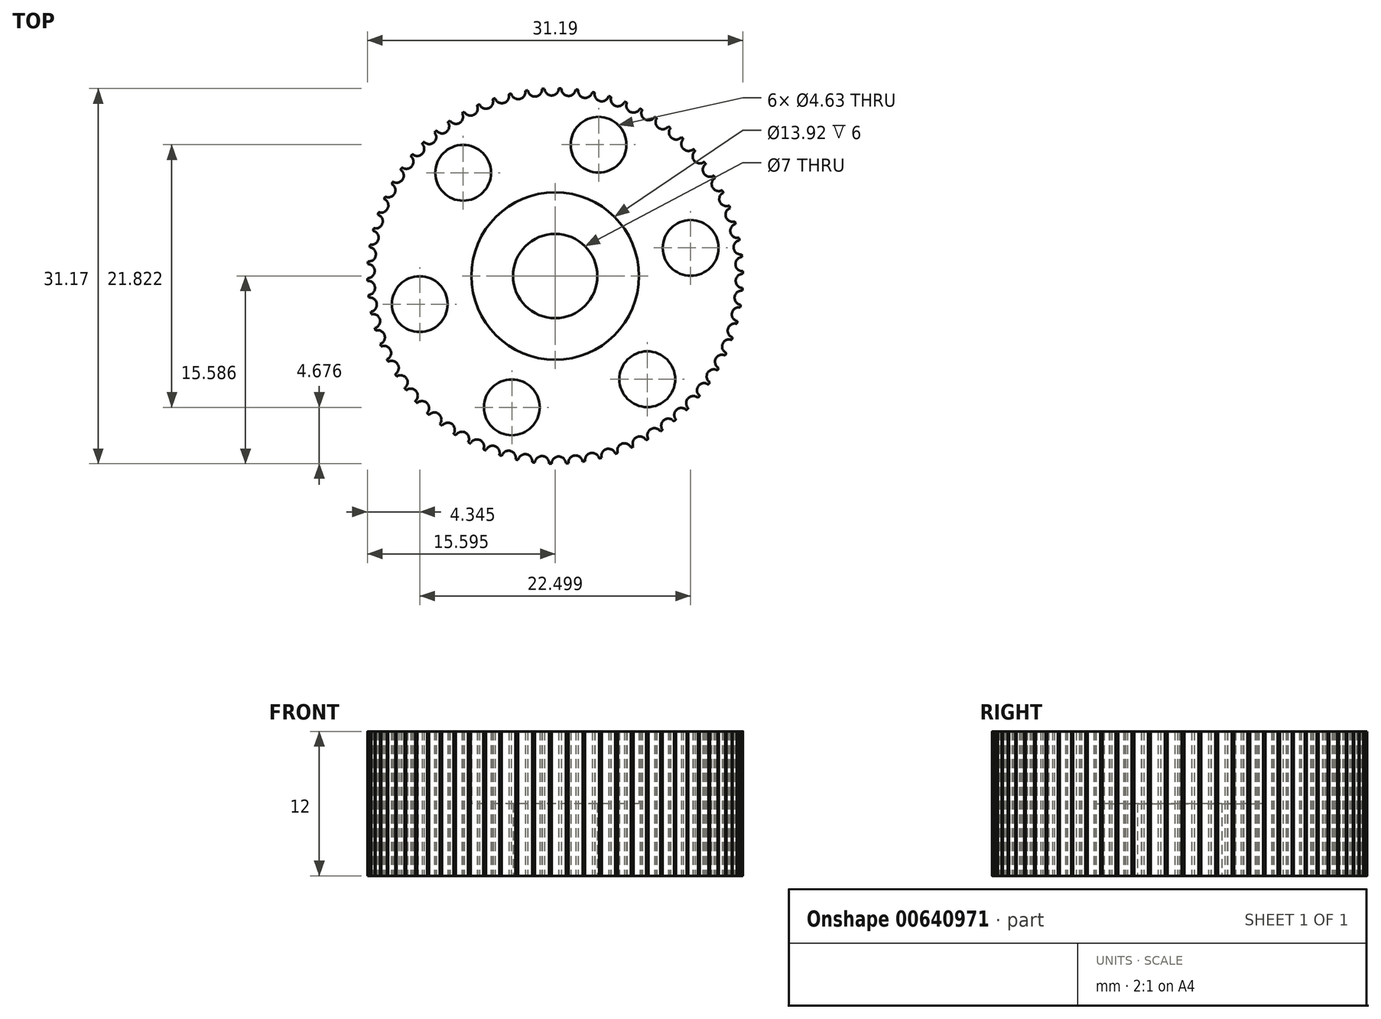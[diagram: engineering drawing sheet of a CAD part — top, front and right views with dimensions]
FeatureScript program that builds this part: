
annotation { "Feature Type Name" : "Feature", "Feature Type Description" : "" }
export const myFeature = defineFeature(function(context is Context, id is Id, definition is map)
    precondition{}
    {
        {
            var Q0;
            Q0=qCreatedBy(makeId("Top.planeOp"),FACE);
            var sketch = newSketch(context, id + "F0", { "sketchPlane" : qUnion([Q0])});
            skCircle(sketch, "E0", {"center": v(-13.85, 5.29) * mm, "radius": 0.6 * mm});
            skCircle(sketch, "E1.1.0", {"center": v(-14.2, 3.93) * mm, "radius": 0.6 * mm});
            skCircle(sketch, "E1.2.0", {"center": v(-14.42, 2.55) * mm, "radius": 0.6 * mm});
            skCircle(sketch, "E1.3.0", {"center": v(-14.52, 1.16) * mm, "radius": 0.6 * mm});
            skCircle(sketch, "E1.4.0", {"center": v(-14.5, -0.24) * mm, "radius": 0.6 * mm});
            skCircle(sketch, "E1.5.0", {"center": v(-14.34, -1.63) * mm, "radius": 0.6 * mm});
            skCircle(sketch, "E1.6.0", {"center": v(-14.07, -3) * mm, "radius": 0.6 * mm});
            skCircle(sketch, "E1.7.0", {"center": v(-13.67, -4.35) * mm, "radius": 0.6 * mm});
            skCircle(sketch, "E1.8.0", {"center": v(-13.15, -5.65) * mm, "radius": 0.6 * mm});
            skCircle(sketch, "E1.9.0", {"center": v(-12.52, -6.9) * mm, "radius": 0.6 * mm});
            skCircle(sketch, "E1.10.0", {"center": v(-11.78, -8.08) * mm, "radius": 0.6 * mm});
            skCircle(sketch, "E1.11.0", {"center": v(-10.94, -9.2) * mm, "radius": 0.6 * mm});
            skCircle(sketch, "E1.12.0", {"center": v(-10, -10.24) * mm, "radius": 0.6 * mm});
            skCircle(sketch, "E1.13.0", {"center": v(-8.97, -11.18) * mm, "radius": 0.6 * mm});
            skCircle(sketch, "E1.14.0", {"center": v(-7.86, -12.04) * mm, "radius": 0.6 * mm});
            skCircle(sketch, "E1.15.0", {"center": v(-6.68, -12.78) * mm, "radius": 0.6 * mm});
            skCircle(sketch, "E1.16.0", {"center": v(-5.44, -13.42) * mm, "radius": 0.6 * mm});
            skCircle(sketch, "E1.17.0", {"center": v(-4.14, -13.95) * mm, "radius": 0.6 * mm});
            skCircle(sketch, "E1.18.0", {"center": v(-2.8, -14.36) * mm, "radius": 0.6 * mm});
            skCircle(sketch, "E1.19.0", {"center": v(-1.43, -14.64) * mm, "radius": 0.6 * mm});
            skCircle(sketch, "E1.20.0", {"center": v(-0.04, -14.8) * mm, "radius": 0.6 * mm});
            skCircle(sketch, "E1.21.0", {"center": v(1.36, -14.84) * mm, "radius": 0.6 * mm});
            skCircle(sketch, "E1.22.0", {"center": v(2.75, -14.75) * mm, "radius": 0.6 * mm});
            skCircle(sketch, "E1.23.0", {"center": v(4.13, -14.54) * mm, "radius": 0.6 * mm});
            skCircle(sketch, "E1.24.0", {"center": v(5.5, -14.2) * mm, "radius": 0.6 * mm});
            skCircle(sketch, "E1.25.0", {"center": v(6.81, -13.75) * mm, "radius": 0.6 * mm});
            skCircle(sketch, "E1.26.0", {"center": v(8.1, -13.17) * mm, "radius": 0.6 * mm});
            skCircle(sketch, "E1.27.0", {"center": v(9.31, -12.49) * mm, "radius": 0.6 * mm});
            skCircle(sketch, "E1.28.0", {"center": v(10.46, -11.7) * mm, "radius": 0.6 * mm});
            skCircle(sketch, "E1.29.0", {"center": v(11.54, -10.8) * mm, "radius": 0.6 * mm});
            skCircle(sketch, "E1.30.0", {"center": v(12.53, -9.82) * mm, "radius": 0.6 * mm});
            skCircle(sketch, "E1.31.0", {"center": v(13.43, -8.75) * mm, "radius": 0.6 * mm});
            skCircle(sketch, "E1.32.0", {"center": v(14.24, -7.6) * mm, "radius": 0.6 * mm});
            skCircle(sketch, "E1.33.0", {"center": v(14.93, -6.38) * mm, "radius": 0.6 * mm});
            skCircle(sketch, "E1.34.0", {"center": v(15.51, -5.11) * mm, "radius": 0.6 * mm});
            skCircle(sketch, "E1.35.0", {"center": v(15.98, -3.8) * mm, "radius": 0.6 * mm});
            skCircle(sketch, "E1.36.0", {"center": v(16.33, -2.44) * mm, "radius": 0.6 * mm});
            skCircle(sketch, "E1.37.0", {"center": v(16.55, -1.06) * mm, "radius": 0.6 * mm});
            skCircle(sketch, "E1.38.0", {"center": v(16.65, 0.34) * mm, "radius": 0.6 * mm});
            skCircle(sketch, "E1.39.0", {"center": v(16.62, 1.74) * mm, "radius": 0.6 * mm});
            skCircle(sketch, "E1.40.0", {"center": v(16.47, 3.13) * mm, "radius": 0.6 * mm});
            skCircle(sketch, "E1.41.0", {"center": v(16.2, 4.5) * mm, "radius": 0.6 * mm});
            skCircle(sketch, "E1.42.0", {"center": v(15.8, 5.84) * mm, "radius": 0.6 * mm});
            skCircle(sketch, "E1.43.0", {"center": v(15.28, 7.14) * mm, "radius": 0.6 * mm});
            skCircle(sketch, "E1.44.0", {"center": v(14.65, 8.39) * mm, "radius": 0.6 * mm});
            skCircle(sketch, "E1.45.0", {"center": v(13.91, 9.58) * mm, "radius": 0.6 * mm});
            skCircle(sketch, "E1.46.0", {"center": v(13.07, 10.7) * mm, "radius": 0.6 * mm});
            skCircle(sketch, "E1.47.0", {"center": v(12.13, 11.73) * mm, "radius": 0.6 * mm});
            skCircle(sketch, "E1.48.0", {"center": v(11.1, 12.68) * mm, "radius": 0.6 * mm});
            skCircle(sketch, "E1.49.0", {"center": v(10, 13.53) * mm, "radius": 0.6 * mm});
            skCircle(sketch, "E1.50.0", {"center": v(8.81, 14.28) * mm, "radius": 0.6 * mm});
            skCircle(sketch, "E1.51.0", {"center": v(7.57, 14.92) * mm, "radius": 0.6 * mm});
            skCircle(sketch, "E1.52.0", {"center": v(6.27, 15.44) * mm, "radius": 0.6 * mm});
            skCircle(sketch, "E1.53.0", {"center": v(4.93, 15.85) * mm, "radius": 0.6 * mm});
            skCircle(sketch, "E1.54.0", {"center": v(3.56, 16.14) * mm, "radius": 0.6 * mm});
            skCircle(sketch, "E1.55.0", {"center": v(2.17, 16.3) * mm, "radius": 0.6 * mm});
            skCircle(sketch, "E1.56.0", {"center": v(0.77, 16.33) * mm, "radius": 0.6 * mm});
            skCircle(sketch, "E1.57.0", {"center": v(-0.62, 16.25) * mm, "radius": 0.6 * mm});
            skCircle(sketch, "E1.58.0", {"center": v(-2, 16.03) * mm, "radius": 0.6 * mm});
            skCircle(sketch, "E1.59.0", {"center": v(-3.36, 15.7) * mm, "radius": 0.6 * mm});
            skCircle(sketch, "E1.60.0", {"center": v(-4.68, 15.24) * mm, "radius": 0.6 * mm});
            skCircle(sketch, "E1.61.0", {"center": v(-5.96, 14.66) * mm, "radius": 0.6 * mm});
            skCircle(sketch, "E1.62.0", {"center": v(-7.18, 13.98) * mm, "radius": 0.6 * mm});
            skCircle(sketch, "E1.63.0", {"center": v(-8.33, 13.19) * mm, "radius": 0.6 * mm});
            skCircle(sketch, "E1.64.0", {"center": v(-9.41, 12.3) * mm, "radius": 0.6 * mm});
            skCircle(sketch, "E1.65.0", {"center": v(-10.4, 11.3) * mm, "radius": 0.6 * mm});
            skCircle(sketch, "E1.66.0", {"center": v(-11.3, 10.24) * mm, "radius": 0.6 * mm});
            skCircle(sketch, "E1.67.0", {"center": v(-12.1, 9.1) * mm, "radius": 0.6 * mm});
            skCircle(sketch, "E1.68.0", {"center": v(-12.8, 7.88) * mm, "radius": 0.6 * mm});
            skCircle(sketch, "E1.69.0", {"center": v(-13.38, 6.6) * mm, "radius": 0.6 * mm});
            skPoint(sketch, "E1.center", {"position": v(1.07, 0.75) * mm});
            skCircle(sketch, "E2", {"center": v(1.07, 0.75) * mm, "radius": 15.6 * mm});
            skCircle(sketch, "E3", {"center": v(1.07, 0.75) * mm, "radius": 3.5 * mm});
            skPoint(sketch, "E4.2.0", {"position": v(0, 0) * mm});
            skPoint(sketch, "E4.3.0", {"position": v(0, 0) * mm});
            skPoint(sketch, "E4.6.0", {"position": v(0, 0) * mm});
            skCircle(sketch, "E5", {"center": v(1.07, 0.75) * mm, "radius": 6.96 * mm});
            skCircle(sketch, "E6", {"center": v(-6.58, 9.32) * mm, "radius": 2.32 * mm});
            skCircle(sketch, "E7.1.0", {"center": v(-10.18, -1.6) * mm, "radius": 2.32 * mm});
            skCircle(sketch, "E7.2.0", {"center": v(-2.54, -10.16) * mm, "radius": 2.32 * mm});
            skCircle(sketch, "E7.3.0", {"center": v(8.71, -7.83) * mm, "radius": 2.32 * mm});
            skCircle(sketch, "E7.4.0", {"center": v(12.31, 3.08) * mm, "radius": 2.32 * mm});
            skCircle(sketch, "E7.5.0", {"center": v(4.67, 11.66) * mm, "radius": 2.32 * mm});
            skSolve(sketch);
        }
        {
            var Q0;
            {var subQ0=sQuery(id+"F0.wireOp",EDGE,"E2");var subQ180=sQuery(id+"F0.wireOp",EDGE,"E0");var subQ186=makeQuery(id+"F0.imprint","INTERSECT",VERTEX,{"disambiguationData":[OD(0.0)],"derivedFrom":[subQ180,subQ0]});Q0=makeQuery(id+"F0.imprint","IMPRINT",FACE,{"disambiguationData":[TD([[makeQuery(id+"F0.imprint","IMPRINT",EDGE,{"disambiguationData":[TD([[subQ186,1.0]])],"derivedFrom":subQ180}),-1.0]])]});}
            extrude(context, id + "F1", {"entities" : qUnion([Q0]), "depth" : 12 * mm, "offsetDistance" : 25.4 * mm});
        }
        {
            var Q0;
            Q0=makeQuery(id+"F0.imprint","IMPRINT",FACE,{"disambiguationData":[TD([[makeQuery(id+"F0.imprint","IMPRINT",EDGE,{"derivedFrom":sQuery(id+"F0.wireOp",EDGE,"E3")}),-1.0]])]});
            extrude(context, id + "F2", {"entities" : qUnion([Q0]), "operationType" : NewBodyOperationType.ADD, "depth" : 6 * mm, "offsetDistance" : 25.4 * mm});
        }
    });
